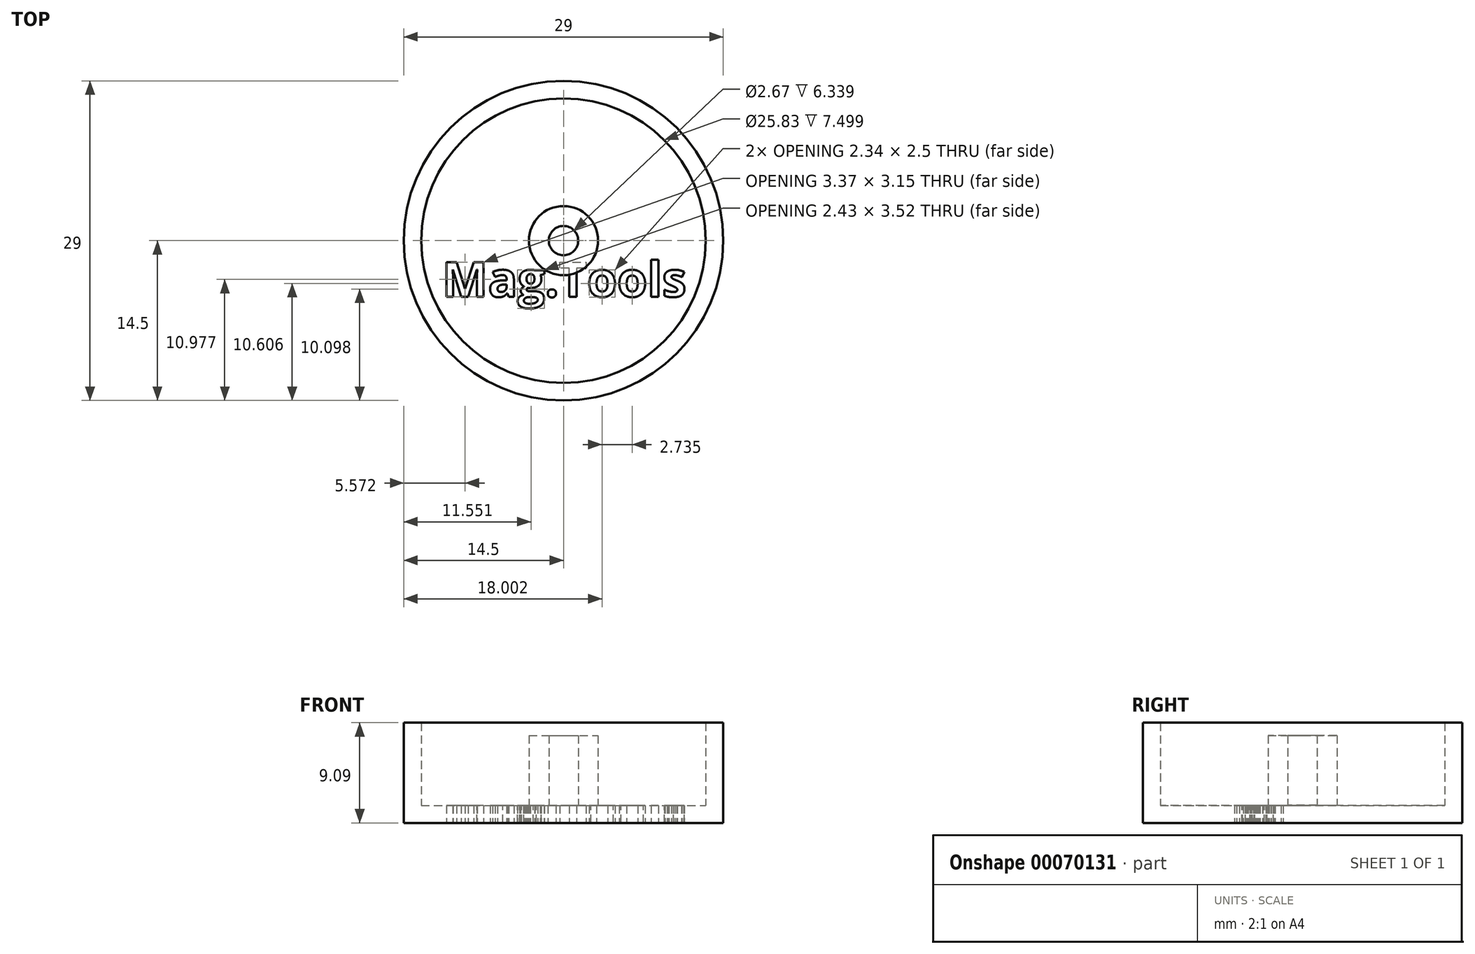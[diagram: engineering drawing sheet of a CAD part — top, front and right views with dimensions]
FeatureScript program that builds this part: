
annotation { "Feature Type Name" : "Feature", "Feature Type Description" : "" }
export const myFeature = defineFeature(function(context is Context, id is Id, definition is map)
    precondition{}
    {
        {
            var Q0;
            Q0=qCreatedBy(makeId("Front.planeOp"),FACE);
            var sketch = newSketch(context, id + "F0", { "sketchPlane" : qUnion([Q0])});
            skLineSegment(sketch, "E0", {"start": v(0, 0) * mm, "end": v(-14.5, 0) * mm});
            skLineSegment(sketch, "E1", {"start": v(-14.5, 0) * mm, "end": v(-14.5, 9.09) * mm});
            skLineSegment(sketch, "E2", {"start": v(-14.5, 9.09) * mm, "end": v(-12.92, 9.09) * mm});
            skLineSegment(sketch, "E3", {"start": v(-12.92, 9.09) * mm, "end": v(-12.92, 1.59) * mm});
            skLineSegment(sketch, "E4", {"start": v(0, 0) * mm, "end": v(0, 1.6) * mm});
            skLineSegment(sketch, "E5", {"start": v(0, 1.6) * mm, "end": v(-1.33, 1.6) * mm});
            skLineSegment(sketch, "E6", {"start": v(-1.33, 1.6) * mm, "end": v(-1.33, 7.93) * mm});
            skLineSegment(sketch, "E7", {"start": v(-1.33, 7.93) * mm, "end": v(-3.14, 7.93) * mm});
            skLineSegment(sketch, "E8", {"start": v(-3.14, 7.93) * mm, "end": v(-3.14, 1.59) * mm});
            skLineSegment(sketch, "E9", {"start": v(-3.14, 1.59) * mm, "end": v(-12.92, 1.59) * mm});
            skSolve(sketch);
        }
        {
            var Q0;
            Q0 = qSketchRegion(id + "F0", true);
            var Q1;
            Q1=sQuery(id+"F0.wireOp",EDGE,"E4");
            revolve(context, id + "F1", {"entities" : qUnion([Q0]), "axis" : qUnion([Q1]), "revolveType" : RevolveType.FULL});
        }
        {
            var Q0;
            Q0=qCreatedBy(makeId("Top.planeOp"),FACE);
            var sketch = newSketch(context, id + "F2", { "sketchPlane" : qUnion([Q0])});
            skText(sketch, "E10", { "text": "Mag.Tools", "fontName": "OpenSans-Bold.ttf"});
            const initialGuessF2  = {"E10": [-0.01101, -0.0051, 1, 0, 0.00318]};
            skSetInitialGuess(sketch, initialGuessF2);
            skSolve(sketch);
        }
        {
            var Q0;
            Q0 = qSketchRegion(id + "F2", true);
            extrude(context, id + "F3", {"entities" : qUnion([Q0]), "operationType" : NewBodyOperationType.REMOVE, "depth" : 1.59 * mm});
        }
    });
